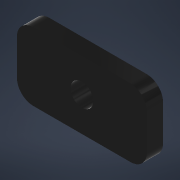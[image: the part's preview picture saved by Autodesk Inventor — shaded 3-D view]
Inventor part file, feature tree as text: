
AUTODESK INVENTOR PART (.ipt)
format: ipt  version: 2021 (Build 250183000, 183)  size: 106,496 bytes
history: native  units: mm
features: other x5, reference x2, extrude x1
ambient origin geometry x8: Origin, YZ Plane, XZ Plane, XY Plane, X Axis, Y Axis, Z Axis, Center Point
bodies: Solid1 (feature_tree)
feature tree (8):
  extrude  "washer"  Depth=16.0mm
  other  "washer_sketch"
  reference  "Reference1"
  reference  "Reference2"
  other  "<userpath>\Documents\Dev\tco-cad\camera_mount\assembly_camera_mount.iam"
  other  "assembly_camera_mount.iam"
  other  "linear_stepper_base:1"
  other  "mount_linear_stepper:1"
